# Revit family: Viking Roofspec Scupper 04 M15
name_source: partatom
category: Pipe Fittings
units: mm (PartAtom-declared; Revit-internal decimal feet)

## family parameters
Cut with Voids When Loaded = Yes
Host = Face
Part Type = Cap
Round Connector Dimension = Use Diameter
Shared = No

## types (1)
- Scuppers - 200mm x 80mm Overflow
    Component = STP604
    Default Elevation = 0 mm  [stored 0 ft]
    Flange Cut Length = 5 mm  [stored 0.0164042 ft]
    Flange Cut Width = 5 mm  [stored 0.0164042 ft]
    Leg Cut Height = 80 mm  [stored 0.262467 ft]
    Leg Cut Offset = 45 mm  [stored 0.147638 ft]
    Leg Cut Width = 200 mm  [stored 0.656168 ft]
    Manufacturer = Viking Roofspec
    Material = Viking Roofspec - Rubber/PVC White
    Model = STP604
    Type Comments = Viking Roofspec 200x80mm TPO overflow scupper STP604, installed as per manufacturers instructions.
    URL = www.vikingroofspec.co.nz

note: [stored X ft] marks values corroborated as IEEE doubles in the binary element streams (Revit-internal decimal feet)

## geometry (parser evidence)
native form markers: Sweep x27
no freeform markers — native parametric forms only
